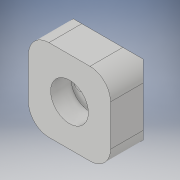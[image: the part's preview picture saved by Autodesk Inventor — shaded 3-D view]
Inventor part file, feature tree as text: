
AUTODESK INVENTOR PART (.ipt)
format: ipt  version: 2017 SP1 (Build 210196100, 196)  size: 141,824 bytes
history: native  units: in
note: dims shown in document units (in); Inventor stores cm internally (conversion verified against a paired STEP export)
features: sketch x3, extrude x2, hole x1, chamfer x1, fillet x1
ambient origin geometry x8: Origin, YZ Plane, XZ Plane, XY Plane, X Axis, Y Axis, Z Axis, Center Point
bodies: Solid1 (feature_tree)
feature tree (8):
  extrude  "Extrusion1"  Depth=0.5in
  extrude  "Extrusion2"  Depth=0.25in
  hole  "Hole1"  [1 undecoded]
  chamfer  "Chamfer2"  Distance=0.05in
  fillet  "Fillet1"  Radius=0.0625in
  sketch  "Sketch1"  dims[d0=0.5in d1=0.5in]
  sketch  "Sketch2"  dims[d2=0.25in d3=0.0in d4=0.23in]
  sketch  "Sketch3"  dims[d5=0.125in d6=0.0in d7=0.05in d8=0.05in d9=0.0625in d10=0.0625in d11=0.075in d12=0.075in d13=0.75in d14=0.375in d15=0.25in d16=0.5635in d17=1.0in d18=0.8108in d22=0.05in d23=0.125in d24=45.0deg d25=0.125in]
note: 1 required parameter value undecoded (feature->parameter linkage not recoverable at this tier; creation-order binding heuristic only, values carry confidence <= 0.55)
